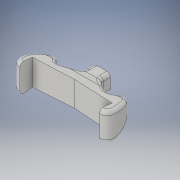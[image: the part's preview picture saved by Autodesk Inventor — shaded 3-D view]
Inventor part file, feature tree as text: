
AUTODESK INVENTOR PART (.ipt)
format: ipt  version: 2017 (Build 210142000, 142)  size: 428,544 bytes
history: native  units: in
note: dims shown in document units (in); Inventor stores cm internally (conversion verified against a paired STEP export)
features: extrude x4, sketch x3, fillet x1, projected_geometry x1
ambient origin geometry x8: Origin, YZ Plane, XZ Plane, XY Plane, X Axis, Y Axis, Z Axis, Center Point
bodies: Solid1 (feature_tree)
feature tree (9):
  extrude  "Extrusion1"  Depth=2.25in
  extrude  "Extrusion2"  Depth=0.3287in
  sketch  "Sketch3"  dims[d5=0.4724in d6=0.0in d7=0.4724in d9=15.748in d10=0.0in d11=15.748in d12=15.748in d13=0.0in d14=0.5in d15=0.5in d16=0.4724in d17=15.748in d19=0.1in]
  extrude  "Extrusion3"  Depth=0.4724in
  extrude  "Extrusion4"  Depth=15.748in TaperAngle=0.0deg
  fillet  "Fillet2"  Radius=15.748in
  sketch  "Sketch1"  dims[d0=0.7874in d1=0.0in d2=2.25in]
  sketch  "Sketch2"  dims[d3=0.3543in d4=0.3287in]
  projected_geometry  "Projected Loop1"
